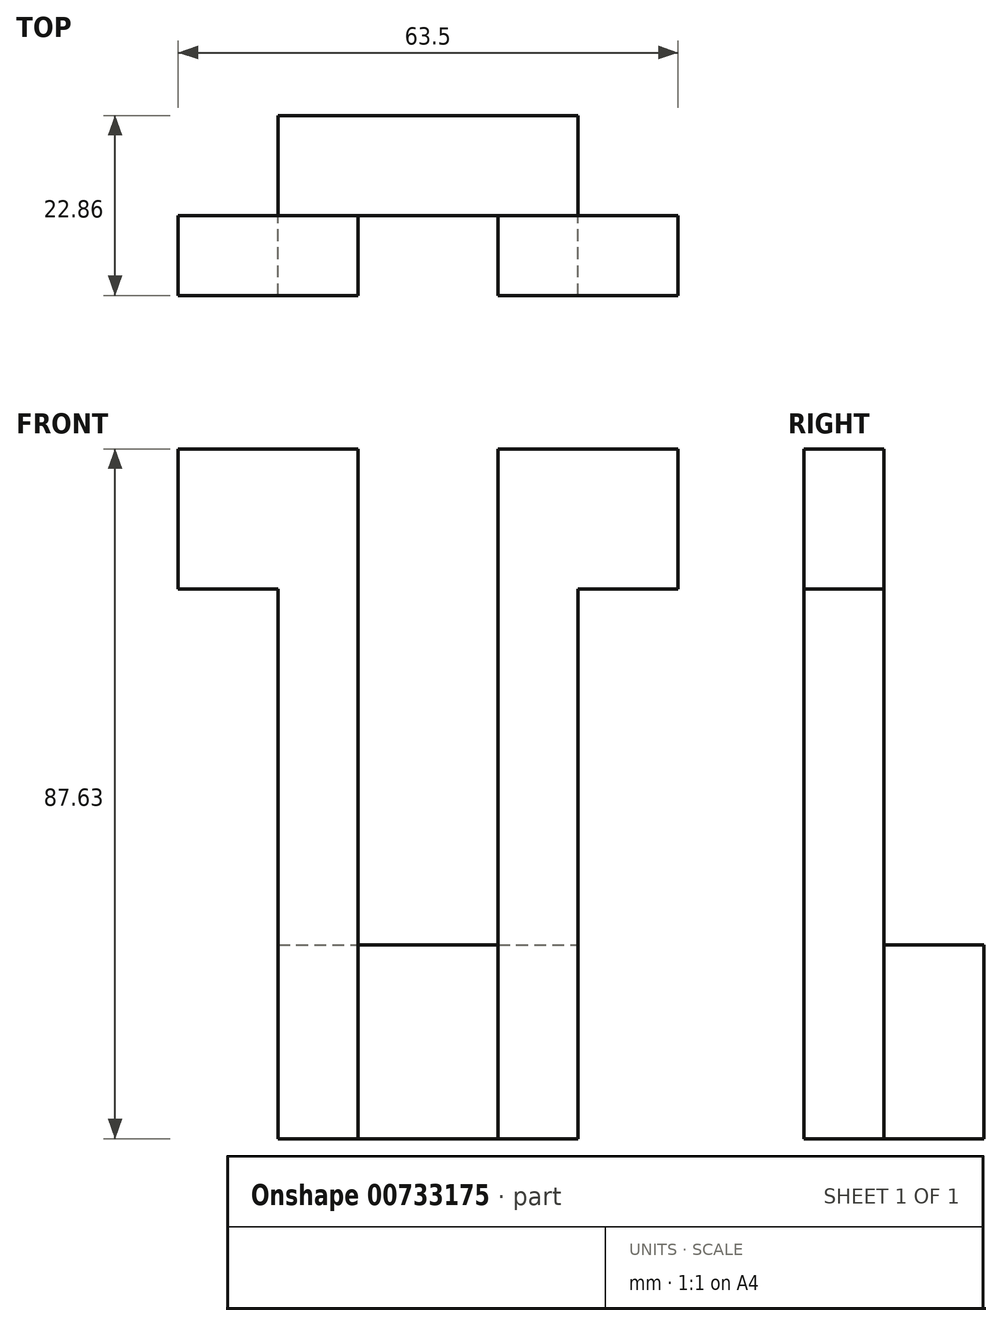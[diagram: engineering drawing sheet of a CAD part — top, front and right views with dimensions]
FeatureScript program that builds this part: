
annotation { "Feature Type Name" : "Feature", "Feature Type Description" : "" }
export const myFeature = defineFeature(function(context is Context, id is Id, definition is map)
    precondition{}
    {
        {
            var Q0;
            Q0=qCreatedBy(makeId("Front.planeOp"),FACE);
            var sketch = newSketch(context, id + "F0", { "sketchPlane" : qUnion([Q0])});
            skLineSegment(sketch, "E0.bottom", {"start": v(-26.73, 10.35) * mm, "end": v(-14.03, 10.35) * mm});
            skLineSegment(sketch, "E0.top", {"start": v(-26.73, -59.5) * mm, "end": v(-14.03, -59.5) * mm});
            skLineSegment(sketch, "E0.left", {"start": v(-26.73, 10.35) * mm, "end": v(-26.73, -59.5) * mm});
            skLineSegment(sketch, "E0.right", {"start": v(-14.03, 10.35) * mm, "end": v(-14.03, -59.5) * mm});
            skLineSegment(sketch, "E1.bottom", {"start": v(-14.03, 10.35) * mm, "end": v(-3.87, 10.35) * mm});
            skLineSegment(sketch, "E1.top", {"start": v(-14.03, -59.5) * mm, "end": v(-3.87, -59.5) * mm});
            skLineSegment(sketch, "E1.right", {"start": v(-3.87, 10.35) * mm, "end": v(-3.87, -59.5) * mm});
            skLineSegment(sketch, "E2.bottom", {"start": v(-3.87, 10.35) * mm, "end": v(13.9, 10.35) * mm});
            skLineSegment(sketch, "E2.top", {"start": v(-3.87, -59.5) * mm, "end": v(13.9, -59.5) * mm});
            skLineSegment(sketch, "E2.right", {"start": v(13.9, 10.35) * mm, "end": v(13.9, -59.5) * mm});
            skLineSegment(sketch, "E3.bottom", {"start": v(13.9, 10.35) * mm, "end": v(24.07, 10.35) * mm});
            skLineSegment(sketch, "E3.top", {"start": v(13.9, -59.5) * mm, "end": v(24.07, -59.5) * mm});
            skLineSegment(sketch, "E3.right", {"start": v(24.07, 10.35) * mm, "end": v(24.07, -59.5) * mm});
            skLineSegment(sketch, "E4.bottom", {"start": v(24.07, 10.35) * mm, "end": v(36.77, 10.35) * mm});
            skLineSegment(sketch, "E4.top", {"start": v(24.07, -59.5) * mm, "end": v(36.77, -59.5) * mm});
            skLineSegment(sketch, "E4.right", {"start": v(36.77, 10.35) * mm, "end": v(36.77, -59.5) * mm});
            skLineSegment(sketch, "E5.bottom", {"start": v(13.9, 10.35) * mm, "end": v(36.77, 10.35) * mm});
            skLineSegment(sketch, "E5.top", {"start": v(13.9, 28.13) * mm, "end": v(36.77, 28.13) * mm});
            skLineSegment(sketch, "E5.left", {"start": v(13.9, 10.35) * mm, "end": v(13.9, 28.13) * mm});
            skLineSegment(sketch, "E5.right", {"start": v(36.77, 10.35) * mm, "end": v(36.77, 28.13) * mm});
            skLineSegment(sketch, "E6.bottom", {"start": v(-3.87, 10.35) * mm, "end": v(-26.73, 10.35) * mm});
            skLineSegment(sketch, "E6.top", {"start": v(-3.87, 28.13) * mm, "end": v(-26.73, 28.13) * mm});
            skLineSegment(sketch, "E6.left", {"start": v(-3.87, 10.35) * mm, "end": v(-3.87, 28.13) * mm});
            skLineSegment(sketch, "E6.right", {"start": v(-26.73, 10.35) * mm, "end": v(-26.73, 28.13) * mm});
            skLineSegment(sketch, "E7.bottom", {"start": v(-14.03, -59.5) * mm, "end": v(24.07, -59.5) * mm});
            skLineSegment(sketch, "E7.top", {"start": v(-14.03, -34.91) * mm, "end": v(24.07, -34.91) * mm});
            skLineSegment(sketch, "E7.left", {"start": v(-14.03, -59.5) * mm, "end": v(-14.03, -34.91) * mm});
            skLineSegment(sketch, "E7.right", {"start": v(24.07, -59.5) * mm, "end": v(24.07, -34.91) * mm});
            skSolve(sketch);
        }
        {
            var Q0;
            Q0=makeQuery(id+"F0.imprint","IMPRINT",FACE,{"disambiguationData":[TD([[makeQuery(id+"F0.imprint","IMPRINT",EDGE,{"derivedFrom":sQuery(id+"F0.wireOp",EDGE,"E0.bottom")}),1.0]])]});
            var Q1;
            Q1=makeQuery(id+"F0.imprint","IMPRINT",FACE,{"disambiguationData":[TD([[makeQuery(id+"F0.imprint","IMPRINT",EDGE,{"derivedFrom":sQuery(id+"F0.wireOp",EDGE,"E1.top")}),1.0]])]});
            var Q2;
            Q2=makeQuery(id+"F0.imprint","IMPRINT",FACE,{"disambiguationData":[TD([[makeQuery(id+"F0.imprint","IMPRINT",EDGE,{"derivedFrom":sQuery(id+"F0.wireOp",EDGE,"E3.top")}),1.0]])]});
            var Q3;
            Q3=makeQuery(id+"F0.imprint","IMPRINT",FACE,{"disambiguationData":[TD([[makeQuery(id+"F0.imprint","IMPRINT",EDGE,{"derivedFrom":sQuery(id+"F0.wireOp",EDGE,"E3.bottom")}),1.0]])]});
            var Q4;
            {var subQ0=sQuery(id+"F0.wireOp",EDGE,"E1.bottom");Q4=makeQuery(id+"F0.imprint","IMPRINT",FACE,{"disambiguationData":[TD([[makeQuery(id+"F0.imprint","IMPRINT",EDGE,{"derivedFrom":subQ0}),-1.0]])]});}
            var Q5;
            {var subQ0=sQuery(id+"F0.wireOp",EDGE,"E3.bottom");Q5=makeQuery(id+"F0.imprint","IMPRINT",FACE,{"disambiguationData":[TD([[makeQuery(id+"F0.imprint","IMPRINT",EDGE,{"derivedFrom":subQ0}),-1.0]])]});}
            var Q6;
            {var subQ0=sQuery(id+"F0.wireOp",EDGE,"E3.top");Q6=makeQuery(id+"F0.imprint","IMPRINT",FACE,{"disambiguationData":[TD([[makeQuery(id+"F0.imprint","IMPRINT",EDGE,{"derivedFrom":subQ0}),1.0]])]});}
            var Q7;
            {var subQ0=sQuery(id+"F0.wireOp",EDGE,"E1.top");Q7=makeQuery(id+"F0.imprint","IMPRINT",FACE,{"disambiguationData":[TD([[makeQuery(id+"F0.imprint","IMPRINT",EDGE,{"derivedFrom":subQ0}),1.0]])]});}
            extrude(context, id + "F1", {"entities" : qUnion([Q0, Q1, Q2, Q3, Q4, Q5, Q6, Q7]), "depth" : 10.16 * mm, "offsetDistance" : 25.4 * mm});
        }
        {
            var Q0;
            {var subQ0=sQuery(id+"F0.wireOp",EDGE,"E1.top");Q0=makeQuery(id+"F0.imprint","IMPRINT",FACE,{"disambiguationData":[TD([[makeQuery(id+"F0.imprint","IMPRINT",EDGE,{"derivedFrom":subQ0}),1.0]])]});}
            var Q1;
            {var subQ0=sQuery(id+"F0.wireOp",EDGE,"E2.top");Q1=makeQuery(id+"F0.imprint","IMPRINT",FACE,{"disambiguationData":[TD([[makeQuery(id+"F0.imprint","IMPRINT",EDGE,{"derivedFrom":subQ0}),1.0]])]});}
            var Q2;
            {var subQ0=sQuery(id+"F0.wireOp",EDGE,"E3.top");Q2=makeQuery(id+"F0.imprint","IMPRINT",FACE,{"disambiguationData":[TD([[makeQuery(id+"F0.imprint","IMPRINT",EDGE,{"derivedFrom":subQ0}),1.0]])]});}
            extrude(context, id + "F2", {"entities" : qUnion([Q0, Q1, Q2]), "oppositeDirection" : true, "depth" : 12.7 * mm, "offsetDistance" : 25.4 * mm});
        }
    });
